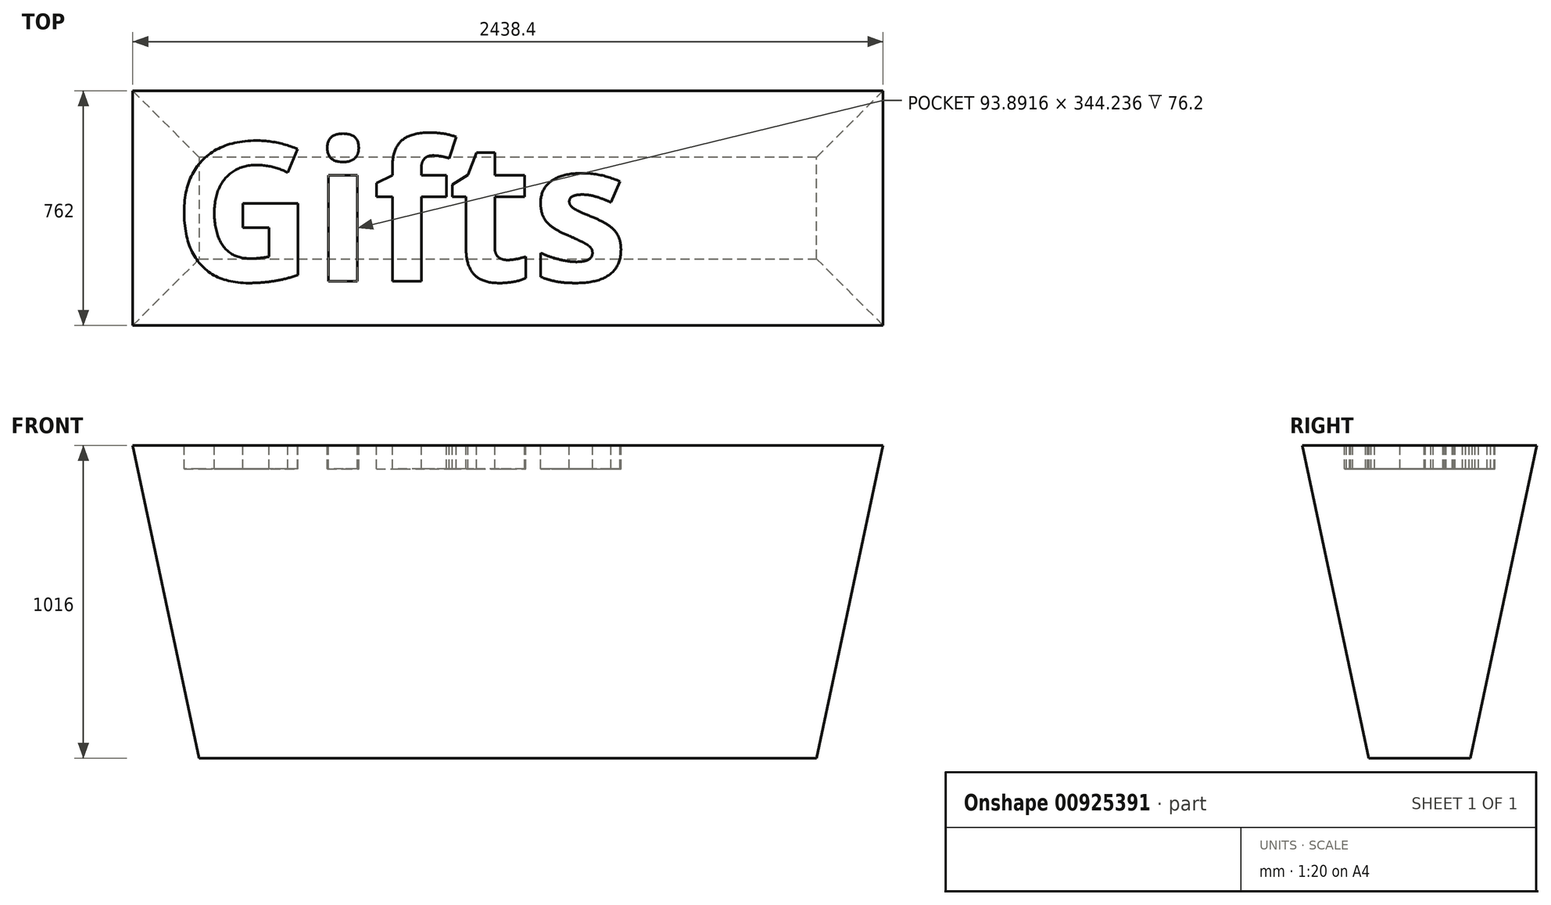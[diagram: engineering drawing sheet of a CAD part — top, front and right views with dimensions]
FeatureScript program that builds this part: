
annotation { "Feature Type Name" : "Feature", "Feature Type Description" : "" }
export const myFeature = defineFeature(function(context is Context, id is Id, definition is map)
    precondition{}
    {
        {
            var Q0;
            Q0=qCreatedBy(makeId("Top.planeOp"),FACE);
            var sketch = newSketch(context, id + "F0", { "sketchPlane" : qUnion([Q0])});
            skLineSegment(sketch, "E0.bottom", {"start": v(1219.2, -381) * mm, "end": v(-1219.2, -381) * mm});
            skLineSegment(sketch, "E0.top", {"start": v(1219.2, 381) * mm, "end": v(-1219.2, 381) * mm});
            skLineSegment(sketch, "E0.left", {"start": v(1219.2, -381) * mm, "end": v(1219.2, 381) * mm});
            skLineSegment(sketch, "E0.right", {"start": v(-1219.2, -381) * mm, "end": v(-1219.2, 381) * mm});
            skPoint(sketch, "E0.middle", {"position": v(0, 0) * mm});
            skSolve(sketch);
        }
        {
            var Q0;
            Q0 = qSketchRegion(id + "F0", true);
            extrude(context, id + "F1", {"entities" : qUnion([Q0]), "oppositeDirection" : true, "depth" : 1016 * mm, "offsetDistance" : 25.4 * mm, "hasDraft" : true, "draftAngle" : 12 * degree, "draftPullDirection" : true});
        }
        {
            var Q0;
            Q0=makeQuery(id+"F1.opExtrude","CAP_FACE",FACE,{"disambiguationData":[OSD([sQuery(id+"F0.wireOp",EDGE,"E0.bottom"),sQuery(id+"F0.wireOp",EDGE,"E0.top"),sQuery(id+"F0.wireOp",EDGE,"E0.left"),sQuery(id+"F0.wireOp",EDGE,"E0.right")])],"isStart":true});
            var sketch = newSketch(context, id + "F2", { "sketchPlane" : qUnion([Q0])});
            skText(sketch, "E1", { "text": "Gifts", "fontName": "OpenSans-Bold.ttf"});
            const initialGuessF2  = {"E1": [-1.08882, -0.23715, 1, 0, 0.45399]};
            skSetInitialGuess(sketch, initialGuessF2);
            skSolve(sketch);
        }
        {
            var Q0;
            Q0 = qSketchRegion(id + "F2", true);
            extrude(context, id + "F3", {"entities" : qUnion([Q0]), "operationType" : NewBodyOperationType.REMOVE, "oppositeDirection" : true, "depth" : 76.2 * mm, "offsetDistance" : 25.4 * mm});
        }
    });
